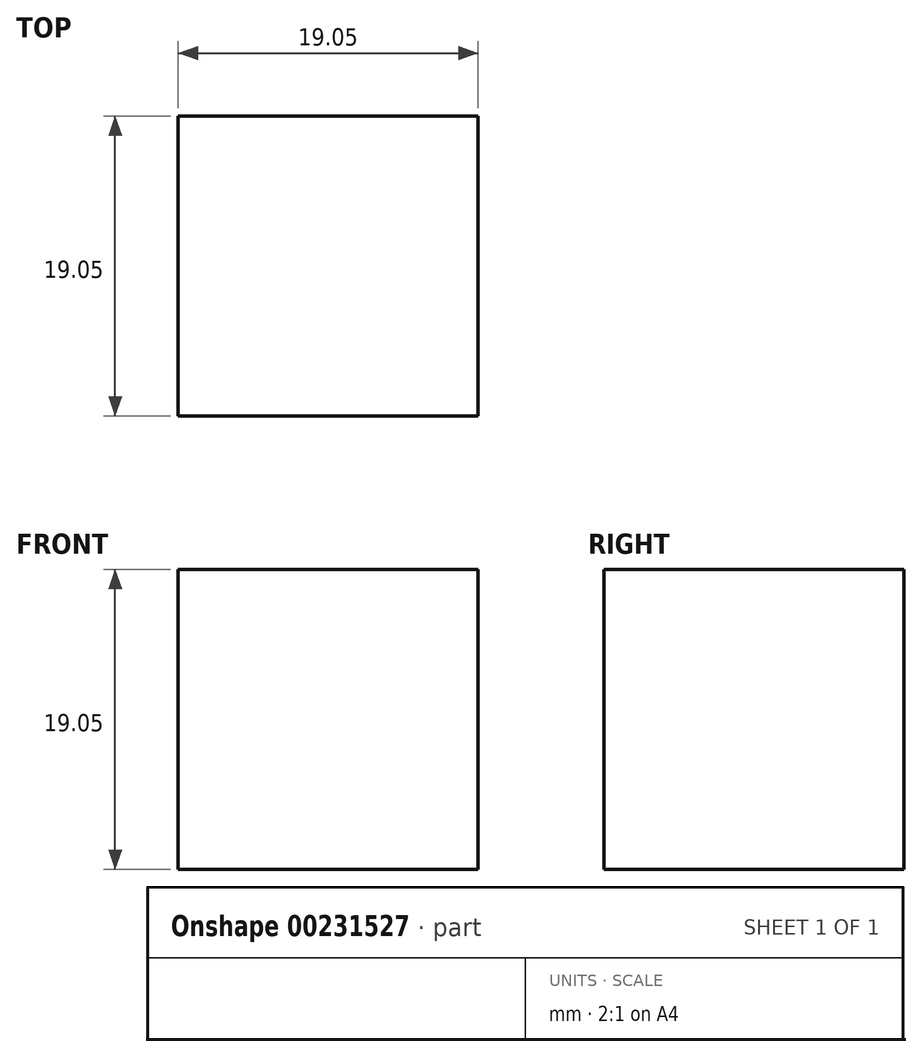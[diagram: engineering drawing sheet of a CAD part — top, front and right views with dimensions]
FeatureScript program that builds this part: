
annotation { "Feature Type Name" : "Feature", "Feature Type Description" : "" }
export const myFeature = defineFeature(function(context is Context, id is Id, definition is map)
    precondition{}
    {
        {
            var Q0;
            Q0=qCreatedBy(makeId("Front.planeOp"),FACE);
            var sketch = newSketch(context, id + "F0", { "sketchPlane" : qUnion([Q0])});
            skLineSegment(sketch, "E0.bottom", {"start": v(-38.63, 45.13) * mm, "end": v(-19.58, 45.13) * mm});
            skLineSegment(sketch, "E0.top", {"start": v(-38.63, 26.08) * mm, "end": v(-19.58, 26.08) * mm});
            skLineSegment(sketch, "E0.left", {"start": v(-38.63, 45.13) * mm, "end": v(-38.63, 26.08) * mm});
            skLineSegment(sketch, "E0.right", {"start": v(-19.58, 45.13) * mm, "end": v(-19.58, 26.08) * mm});
            skSolve(sketch);
        }
        {
            var Q0;
            Q0 = qSketchRegion(id + "F0", true);
            extrude(context, id + "F1", {"entities" : qUnion([Q0]), "depth" : 19.05 * mm});
        }
    });
